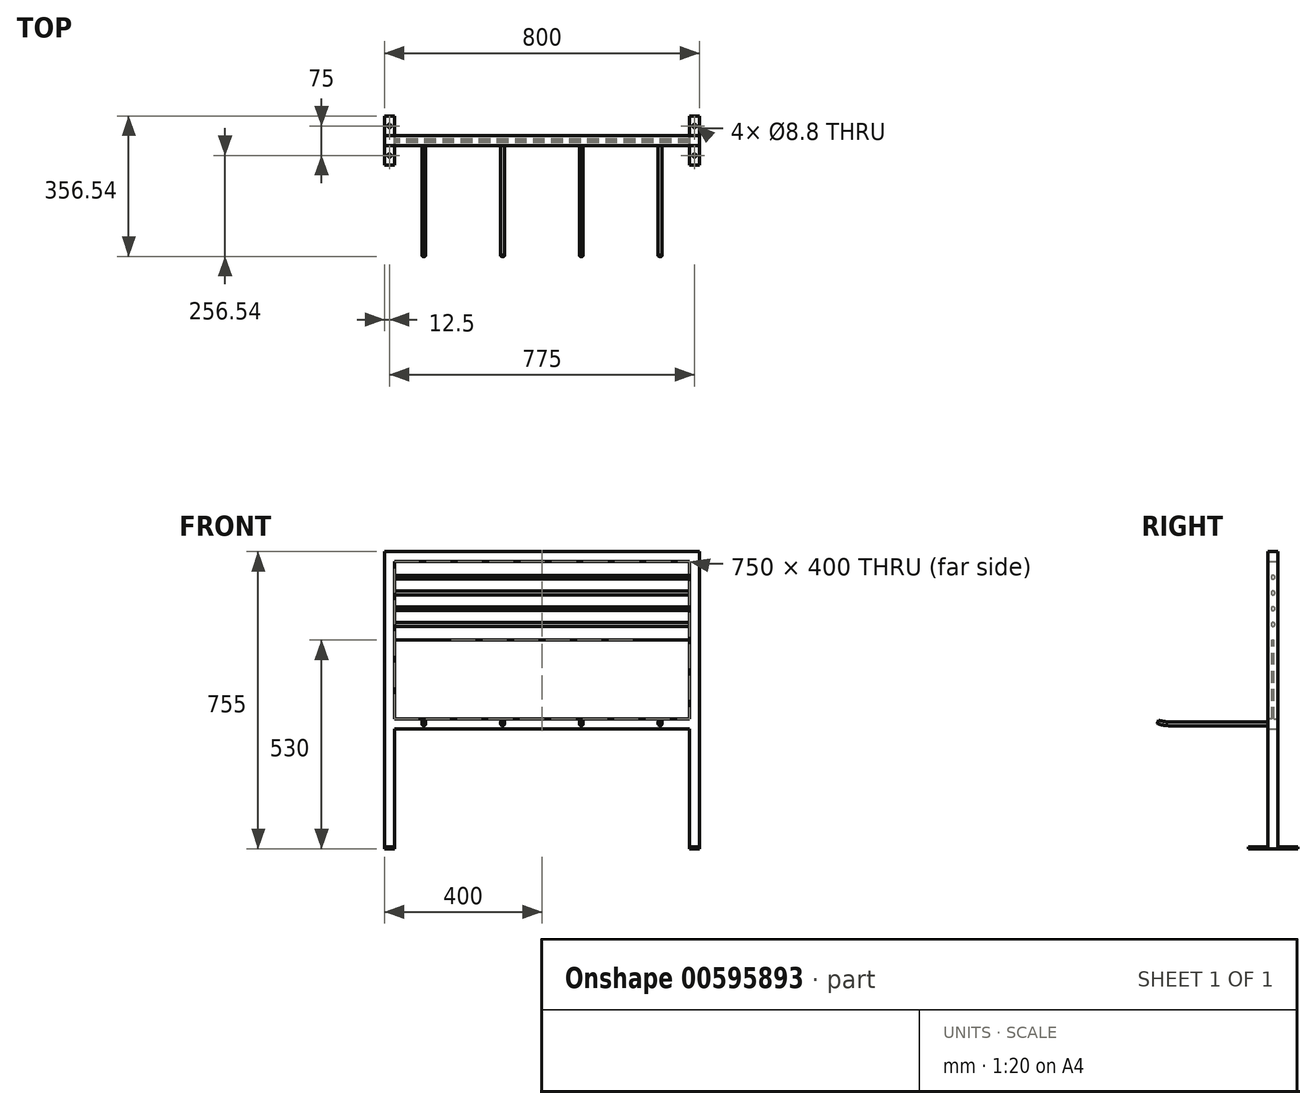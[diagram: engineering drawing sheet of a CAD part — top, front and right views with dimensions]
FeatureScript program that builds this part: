
annotation { "Feature Type Name" : "Feature", "Feature Type Description" : "" }
export const myFeature = defineFeature(function(context is Context, id is Id, definition is map)
    precondition{}
    {
        {
            var Q0;
            Q0=qCreatedBy(makeId("Right.planeOp"),FACE);
            var sketch = newSketch(context, id + "F0", { "sketchPlane" : qUnion([Q0])});
            skLineSegment(sketch, "E0.bottom", {"start": v(12.5, 12.5) * mm, "end": v(-12.5, 12.5) * mm});
            skLineSegment(sketch, "E0.top", {"start": v(12.5, -12.5) * mm, "end": v(-12.5, -12.5) * mm});
            skLineSegment(sketch, "E0.left", {"start": v(12.5, 12.5) * mm, "end": v(12.5, -12.5) * mm});
            skLineSegment(sketch, "E0.right", {"start": v(-12.5, 12.5) * mm, "end": v(-12.5, -12.5) * mm});
            skPoint(sketch, "E0.middle", {"position": v(0, 0) * mm});
            skSolve(sketch);
        }
        {
            var Q0;
            Q0=makeQuery(id+"F0.imprint","IMPRINT",FACE,{"disambiguationData":[TD([[makeQuery(id+"F0.imprint","IMPRINT",EDGE,{"derivedFrom":sQuery(id+"F0.wireOp",EDGE,"E0.bottom")}),1.0]])]});
            extrude(context, id + "F1", {"entities" : qUnion([Q0]), "depth" : 400 * mm, "offsetDistance" : 25.4 * mm, "hasSecondDirection" : true, "secondDirectionOppositeDirection" : true, "secondDirectionDepth" : 400 * mm});
        }
        {
            var Q0;
            Q0=makeQuery(id+"F1.opExtrude","SWEPT_FACE",FACE,{"disambiguationData":[OSD([sQuery(id+"F0.wireOp",EDGE,"E0.right")])]});
            var sketch = newSketch(context, id + "F2", { "sketchPlane" : qUnion([Q0])});
            skLineSegment(sketch, "E1", {"start": v(-400, 0) * mm, "end": v(400, 0) * mm, "construction": true});
            skCircle(sketch, "E2", {"center": v(-100, 0) * mm, "radius": 4.75 * mm});
            skCircle(sketch, "E3", {"center": v(100, 0) * mm, "radius": 4.75 * mm});
            skCircle(sketch, "E4", {"center": v(-300, 0) * mm, "radius": 4.75 * mm});
            skCircle(sketch, "E5", {"center": v(300, 0) * mm, "radius": 4.75 * mm});
            skSolve(sketch);
        }
        {
            var Q0;
            Q0=qCreatedBy(makeId("Right.planeOp"),FACE);
            var sketch = newSketch(context, id + "F3", { "sketchPlane" : qUnion([Q0])});
            skLineSegment(sketch, "E6", {"start": v(-12.5, 0) * mm, "end": v(-262.5, 0) * mm});
            skArc(sketch, "E7", {"start": v(-262.5, 0) * mm, "mid": v(-277.7, 1.26) * mm, "end": v(-292.5, 5) * mm});
            skSolve(sketch);
        }
        {
            var Q0;
            Q0=qSketchRegion(id+"F2",true);
            var Q1;
            Q1=qConstructionFilter(qBodyType(qCreatedBy(id+"F3",EDGE),BodyType.WIRE),ConstructionObject.NO);
            sweep(context, id + "F4", {"operationType" : NewBodyOperationType.ADD, "profiles" : qUnion([Q0]), "path" : qUnion([Q1])});
        }
        {
            var Q0;
            Q0=makeQuery(id+"F1.opExtrude","SWEPT_FACE",FACE,{"disambiguationData":[OSD([sQuery(id+"F0.wireOp",EDGE,"E0.top")])]});
            var sketch = newSketch(context, id + "F5", { "sketchPlane" : qUnion([Q0])});
            skLineSegment(sketch, "E8.bottom", {"start": v(-400, 12.5) * mm, "end": v(-375, 12.5) * mm});
            skLineSegment(sketch, "E8.top", {"start": v(-400, -12.5) * mm, "end": v(-375, -12.5) * mm});
            skLineSegment(sketch, "E8.left", {"start": v(-400, 12.5) * mm, "end": v(-400, -12.5) * mm});
            skLineSegment(sketch, "E8.right", {"start": v(-375, 12.5) * mm, "end": v(-375, -12.5) * mm});
            skLineSegment(sketch, "E9.bottom", {"start": v(400, 12.5) * mm, "end": v(375, 12.5) * mm});
            skLineSegment(sketch, "E9.top", {"start": v(400, -12.5) * mm, "end": v(375, -12.5) * mm});
            skLineSegment(sketch, "E9.left", {"start": v(400, 12.5) * mm, "end": v(400, -12.5) * mm});
            skLineSegment(sketch, "E9.right", {"start": v(375, 12.5) * mm, "end": v(375, -12.5) * mm});
            skSolve(sketch);
        }
        {
            var Q0;
            Q0=qSketchRegion(id+"F5",true);
            extrude(context, id + "F6", {"entities" : qUnion([Q0]), "operationType" : NewBodyOperationType.ADD, "depth" : 300 * mm, "offsetDistance" : 25 * mm});
        }
        {
            var Q0;
            Q0=makeQuery(id+"F6.opExtrude","CAP_FACE",FACE,{"disambiguationData":[OSD([sQuery(id+"F5.wireOp",EDGE,"E9.bottom"),sQuery(id+"F5.wireOp",EDGE,"E9.top"),sQuery(id+"F5.wireOp",EDGE,"E9.left"),sQuery(id+"F5.wireOp",EDGE,"E9.right")])],"isStart":false});
            var sketch = newSketch(context, id + "F7", { "sketchPlane" : qUnion([Q0])});
            skLineSegment(sketch, "E10.0.0", {"start": v(-375, -12.5) * mm, "end": v(-375, 12.5) * mm});
            skLineSegment(sketch, "E10.0.1", {"start": v(-375, 12.5) * mm, "end": v(-400, 12.5) * mm});
            skLineSegment(sketch, "E10.0.2", {"start": v(-400, 12.5) * mm, "end": v(-400, -12.5) * mm});
            skLineSegment(sketch, "E10.0.3", {"start": v(-400, -12.5) * mm, "end": v(-375, -12.5) * mm});
            skLineSegment(sketch, "E11.bottom", {"start": v(-400, 12.5) * mm, "end": v(-375, 12.5) * mm});
            skLineSegment(sketch, "E11.top", {"start": v(-400, 62.5) * mm, "end": v(-375, 62.5) * mm});
            skLineSegment(sketch, "E11.left", {"start": v(-400, 12.5) * mm, "end": v(-400, 62.5) * mm});
            skLineSegment(sketch, "E11.right", {"start": v(-375, 12.5) * mm, "end": v(-375, 62.5) * mm});
            skLineSegment(sketch, "E12.top", {"start": v(-400, -62.5) * mm, "end": v(-375, -62.5) * mm});
            skLineSegment(sketch, "E12.left", {"start": v(-400, -12.5) * mm, "end": v(-400, -62.5) * mm});
            skLineSegment(sketch, "E12.right", {"start": v(-375, -12.5) * mm, "end": v(-375, -62.5) * mm});
            skLineSegment(sketch, "E13.MirrorCS", {"start": v(400, 12.5) * mm, "end": v(375, 12.5) * mm});
            skLineSegment(sketch, "E14.MirrorCS", {"start": v(400, -12.5) * mm, "end": v(375, -12.5) * mm});
            skLineSegment(sketch, "E15.MirrorCS", {"start": v(375, 12.5) * mm, "end": v(400, 12.5) * mm});
            skLineSegment(sketch, "E16.MirrorCS", {"start": v(375, -12.5) * mm, "end": v(375, 12.5) * mm});
            skLineSegment(sketch, "E17.MirrorCS", {"start": v(400, 12.5) * mm, "end": v(400, -12.5) * mm});
            skLineSegment(sketch, "E18.MirrorCS", {"start": v(400, 62.5) * mm, "end": v(375, 62.5) * mm});
            skLineSegment(sketch, "E19.MirrorCS", {"start": v(400, -62.5) * mm, "end": v(375, -62.5) * mm});
            skLineSegment(sketch, "E20.MirrorCS", {"start": v(375, -12.5) * mm, "end": v(375, -62.5) * mm});
            skLineSegment(sketch, "E21.MirrorCS", {"start": v(400, -12.5) * mm, "end": v(400, -62.5) * mm});
            skLineSegment(sketch, "E22.MirrorCS", {"start": v(400, 12.5) * mm, "end": v(400, 62.5) * mm});
            skLineSegment(sketch, "E23.MirrorCS", {"start": v(375, 12.5) * mm, "end": v(375, 62.5) * mm});
            skSolve(sketch);
        }
        {
            var Q0;
            Q0=qSketchRegion(id+"F7",true);
            extrude(context, id + "F8", {"entities" : qUnion([Q0]), "operationType" : NewBodyOperationType.ADD, "depth" : 5 * mm, "offsetDistance" : 25 * mm});
        }
        {
            var Q0;
            Q0=makeQuery(id+"F1.opExtrude","SWEPT_FACE",FACE,{"disambiguationData":[OSD([sQuery(id+"F0.wireOp",EDGE,"E0.bottom")])]});
            var sketch = newSketch(context, id + "F9", { "sketchPlane" : qUnion([Q0])});
            skLineSegment(sketch, "E24.bottom", {"start": v(-400, 12.5) * mm, "end": v(-375, 12.5) * mm});
            skLineSegment(sketch, "E24.top", {"start": v(-400, -12.5) * mm, "end": v(-375, -12.5) * mm});
            skLineSegment(sketch, "E24.left", {"start": v(-400, 12.5) * mm, "end": v(-400, -12.5) * mm});
            skLineSegment(sketch, "E24.right", {"start": v(-375, 12.5) * mm, "end": v(-375, -12.5) * mm});
            skLineSegment(sketch, "E25.bottom", {"start": v(400, -12.5) * mm, "end": v(375, -12.5) * mm});
            skLineSegment(sketch, "E25.top", {"start": v(400, 12.5) * mm, "end": v(375, 12.5) * mm});
            skLineSegment(sketch, "E25.left", {"start": v(400, -12.5) * mm, "end": v(400, 12.5) * mm});
            skLineSegment(sketch, "E25.right", {"start": v(375, -12.5) * mm, "end": v(375, 12.5) * mm});
            skSolve(sketch);
        }
        {
            var Q0;
            Q0 = qSketchRegion(id + "F9", true);
            extrude(context, id + "F10", {"entities" : qUnion([Q0]), "operationType" : NewBodyOperationType.ADD, "depth" : 425 * mm, "offsetDistance" : 25 * mm});
        }
        {
            var Q0;
            Q0=makeQuery(id+"F10.opExtrude","SWEPT_FACE",FACE,{"disambiguationData":[OSD([sQuery(id+"F9.wireOp",EDGE,"E24.right")])]});
            var sketch = newSketch(context, id + "F11", { "sketchPlane" : qUnion([Q0])});
            skLineSegment(sketch, "E26.bottom", {"start": v(-12.5, 437.5) * mm, "end": v(12.5, 437.5) * mm});
            skLineSegment(sketch, "E26.top", {"start": v(-12.5, 412.5) * mm, "end": v(12.5, 412.5) * mm});
            skLineSegment(sketch, "E26.left", {"start": v(-12.5, 437.5) * mm, "end": v(-12.5, 412.5) * mm});
            skLineSegment(sketch, "E26.right", {"start": v(12.5, 437.5) * mm, "end": v(12.5, 412.5) * mm});
            skSolve(sketch);
        }
        {
            var Q0;
            Q0=makeQuery(id+"F11.imprint","IMPRINT",FACE,{"disambiguationData":[TD([[makeQuery(id+"F11.imprint","IMPRINT",EDGE,{"derivedFrom":sQuery(id+"F11.wireOp",EDGE,"E26.bottom")}),1.0]])]});
            extrude(context, id + "F12", {"entities" : qUnion([Q0]), "operationType" : NewBodyOperationType.ADD, "endBound" : BoundingType.UP_TO_NEXT, "depth" : 25 * mm, "offsetDistance" : 25 * mm});
        }
        {
            var Q0;
            Q0=makeQuery(id+"F10.opExtrude","SWEPT_FACE",FACE,{"disambiguationData":[OSD([sQuery(id+"F9.wireOp",EDGE,"E24.right")])]});
            var sketch = newSketch(context, id + "F13", { "sketchPlane" : qUnion([Q0])});
            skLineSegment(sketch, "E27.0", {"start": v(12.5, 12.5) * mm, "end": v(-12.5, 12.5) * mm, "construction": true});
            skLineSegment(sketch, "E28.0", {"start": v(-12.5, 412.5) * mm, "end": v(12.5, 412.5) * mm, "construction": true});
            skLineSegment(sketch, "E29", {"start": v(0, 12.5) * mm, "end": v(0, 412.5) * mm, "construction": true});
            skLineSegment(sketch, "E30.bottom", {"start": v(-2.5, 12.5) * mm, "end": v(2.5, 12.5) * mm});
            skLineSegment(sketch, "E30.top", {"start": v(-2.5, 212.5) * mm, "end": v(2.5, 212.5) * mm});
            skLineSegment(sketch, "E30.left", {"start": v(-2.5, 12.5) * mm, "end": v(-2.5, 212.5) * mm});
            skLineSegment(sketch, "E30.right", {"start": v(2.5, 12.5) * mm, "end": v(2.5, 212.5) * mm});
            skCircle(sketch, "E31", {"center": v(0, 372.5) * mm, "radius": 4.75 * mm});
            skCircle(sketch, "E32.0.1.0", {"center": v(0, 332.5) * mm, "radius": 4.75 * mm});
            skCircle(sketch, "E32.0.2.0", {"center": v(0, 292.5) * mm, "radius": 4.75 * mm});
            skCircle(sketch, "E32.0.3.0", {"center": v(0, 252.5) * mm, "radius": 4.75 * mm});
            skLineSegment(sketch, "E32.direction1", {"start": v(0, 372.5) * mm, "end": v(42.5, 372.5) * mm, "construction": true});
            skLineSegment(sketch, "E32.direction2", {"start": v(0, 372.5) * mm, "end": v(0, 332.5) * mm, "construction": true});
            skSolve(sketch);
        }
        {
            var Q0;
            Q0 = qSketchRegion(id + "F13", true);
            extrude(context, id + "F14", {"entities" : qUnion([Q0]), "operationType" : NewBodyOperationType.ADD, "endBound" : BoundingType.UP_TO_NEXT, "depth" : 25 * mm, "offsetDistance" : 25 * mm});
        }
        {
            var Q0;
            {var subQ0=sQuery(id+"F0.wireOp",EDGE,"E0.right");var subQ1=sQuery(id+"F7.wireOp",EDGE,"E11.top");var subQ2=sQuery(id+"F7.wireOp",EDGE,"E12.right");var subQ3=sQuery(id+"F7.wireOp",EDGE,"E11.right");var subQ4=sQuery(id+"F7.wireOp",EDGE,"E10.0.0");var subQ5=sQuery(id+"F7.wireOp",EDGE,"E12.left");var subQ6=sQuery(id+"F7.wireOp",EDGE,"E11.left");var subQ7=sQuery(id+"F7.wireOp",EDGE,"E10.0.2");Q0=makeQuery(id+"F8.boolean.opBoolean","SPLIT",FACE,{"disambiguationData":[TD([makeQuery(id+"F1.opExtrude","SWEPT_FACE",FACE,{"disambiguationData":[OSD([subQ0])]})])],"derivedFrom":makeQuery(id+"F8.opExtrude","CAP_FACE",FACE,{"disambiguationData":[OSD([subQ4,subQ7,subQ1,subQ6,subQ3,sQuery(id+"F7.wireOp",EDGE,"E12.top"),subQ5,subQ2])],"isStart":true})});}
            var sketch = newSketch(context, id + "F15", { "sketchPlane" : qUnion([Q0])});
            skPoint(sketch, "E33.0", {"position": v(-387.5, -62.5) * mm});
            skPoint(sketch, "E34.0", {"position": v(-387.5, 62.5) * mm});
            skLineSegment(sketch, "E35", {"start": v(-387.5, -62.5) * mm, "end": v(-387.5, 62.5) * mm, "construction": true});
            skPoint(sketch, "E36", {"position": v(-387.5, -37.5) * mm});
            skPoint(sketch, "E37.MirrorP", {"position": v(387.5, -62.5) * mm});
            skPoint(sketch, "E38.MirrorP", {"position": v(387.5, -37.5) * mm});
            skPoint(sketch, "E39.MirrorP", {"position": v(387.5, 37.5) * mm});
            skPoint(sketch, "E40.MirrorP", {"position": v(-387.5, 37.5) * mm});
            skPoint(sketch, "E41.MirrorP", {"position": v(387.5, 62.5) * mm});
            skSolve(sketch);
        }
        {
            var Q0;
            Q0=sQuery(id+"F15.wireOp",VERTEX,"E36");
            var Q1;
            Q1=sQuery(id+"F15.wireOp",VERTEX,"E40.MirrorP");
            var Q2;
            Q2=sQuery(id+"F15.wireOp",VERTEX,"E38.MirrorP");
            var Q3;
            Q3=sQuery(id+"F15.wireOp",VERTEX,"E39.MirrorP");
            var Q4;
            Q4=makeQuery(id+"F1.opExtrude","SWEPT_BODY",BODY,{"disambiguationData":[OSD([sQuery(id+"F0.wireOp",EDGE,"E0.bottom"),sQuery(id+"F0.wireOp",EDGE,"E0.top"),sQuery(id+"F0.wireOp",EDGE,"E0.left"),sQuery(id+"F0.wireOp",EDGE,"E0.right")])]});
            hole(context, id + "F16", {"style" : HoleStyle.SIMPLE, "endStyle" : HoleEndStyle.THROUGH, "standardTappedOrClearance" : lookupTablePath({ "standard" : "ISO", "fit" : "Normal", "size" : "M8", "type" : "Clearance" }), "standardBlindInLast" : lookupTablePath({ "fit" : "Standard", "standard" : "ISO", "size" : "M8", "type" : "Clearance" }), "holeDiameter" : 8.8 * mm, "majorDiameter" : 5 * mm, "isTappedThrough" : true, "tappedDepth" : 12 * mm, "tapClearance" : 3, "startFromSketch" : true, "locations" : qUnion([Q0, Q1, Q2, Q3]), "scope" : qUnion([Q4])});
        }
    });
